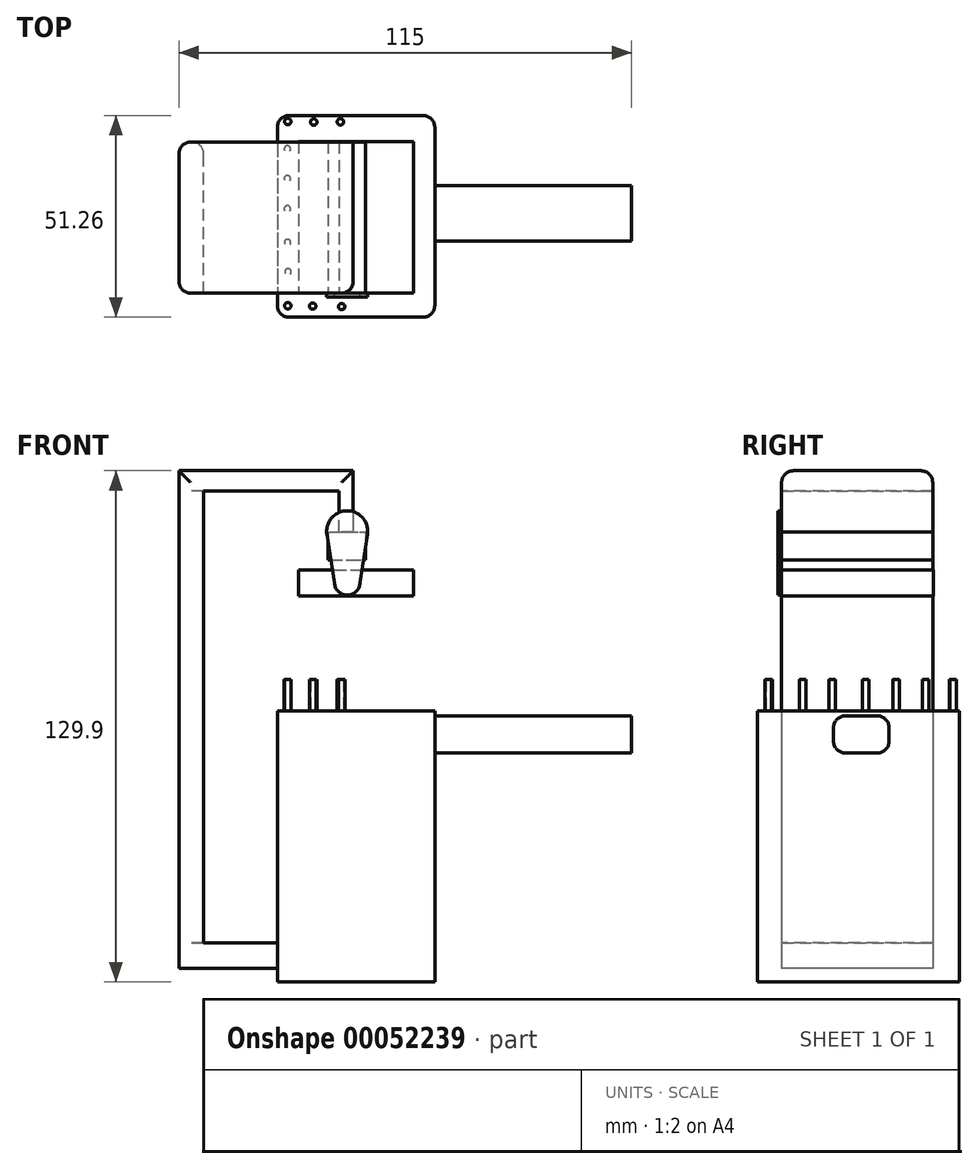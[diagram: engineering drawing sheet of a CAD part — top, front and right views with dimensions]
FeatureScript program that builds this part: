
annotation { "Feature Type Name" : "Feature", "Feature Type Description" : "" }
export const myFeature = defineFeature(function(context is Context, id is Id, definition is map)
    precondition{}
    {
        {
            var Q0;
            Q0=qCreatedBy(makeId("Right.planeOp"),FACE);
            var sketch = newSketch(context, id + "F0", { "sketchPlane" : qUnion([Q0])});
            skLineSegment(sketch, "E0.bottom", {"start": v(7.43, 4.7) * mm, "end": v(-6.69, 4.7) * mm});
            skLineSegment(sketch, "E0.top", {"start": v(7.43, -4.7) * mm, "end": v(-6.69, -4.7) * mm});
            skLineSegment(sketch, "E0.left", {"start": v(7.43, 4.7) * mm, "end": v(7.43, -4.7) * mm});
            skLineSegment(sketch, "E0.right", {"start": v(-6.69, 4.7) * mm, "end": v(-6.69, -4.7) * mm});
            skSolve(sketch);
        }
        {
            var Q0;
            Q0 = qSketchRegion(id + "F0", true);
            extrude(context, id + "F1", {"entities" : qUnion([Q0]), "depth" : 50 * mm});
        }
        {
            var Q0;
            Q0=makeQuery(id+"F1.opExtrude","CAP_FACE",FACE,{"disambiguationData":[OSD([sQuery(id+"F0.wireOp",EDGE,"E0.bottom"),sQuery(id+"F0.wireOp",EDGE,"E0.top"),sQuery(id+"F0.wireOp",EDGE,"E0.left"),sQuery(id+"F0.wireOp",EDGE,"E0.right")])],"isStart":true});
            var sketch = newSketch(context, id + "F2", { "sketchPlane" : qUnion([Q0])});
            skLineSegment(sketch, "E1.bottom", {"start": v(-25.26, 5.94) * mm, "end": v(26, 5.94) * mm});
            skLineSegment(sketch, "E1.top", {"start": v(-25.26, -62.9) * mm, "end": v(26, -62.9) * mm});
            skLineSegment(sketch, "E1.left", {"start": v(-25.26, 5.94) * mm, "end": v(-25.26, -62.9) * mm});
            skLineSegment(sketch, "E1.right", {"start": v(26, 5.94) * mm, "end": v(26, -62.9) * mm});
            skSolve(sketch);
        }
        {
            var Q0;
            Q0 = qSketchRegion(id + "F2", true);
            extrude(context, id + "F3", {"entities" : qUnion([Q0]), "operationType" : NewBodyOperationType.ADD, "depth" : 40 * mm});
        }
        {
            var Q0;
            Q0=makeQuery(id+"F3.opExtrude","CAP_FACE",FACE,{"disambiguationData":[OSD([sQuery(id+"F2.wireOp",EDGE,"E1.bottom"),sQuery(id+"F2.wireOp",EDGE,"E1.top"),sQuery(id+"F2.wireOp",EDGE,"E1.left"),sQuery(id+"F2.wireOp",EDGE,"E1.right")])],"isStart":false});
            var sketch = newSketch(context, id + "F4", { "sketchPlane" : qUnion([Q0])});
            skLineSegment(sketch, "E2.bottom", {"start": v(-18.5, -53) * mm, "end": v(19.88, -53) * mm});
            skLineSegment(sketch, "E2.top", {"start": v(-18.5, -59.44) * mm, "end": v(19.88, -59.44) * mm});
            skLineSegment(sketch, "E2.left", {"start": v(-18.5, -53) * mm, "end": v(-18.5, -59.44) * mm});
            skLineSegment(sketch, "E2.right", {"start": v(19.88, -53) * mm, "end": v(19.88, -59.44) * mm});
            skSolve(sketch);
        }
        {
            var Q0;
            Q0 = qSketchRegion(id + "F4", true);
            extrude(context, id + "F5", {"entities" : qUnion([Q0]), "operationType" : NewBodyOperationType.ADD, "depth" : 25 * mm});
        }
        {
            var Q0;
            Q0=makeQuery(id+"F5.opExtrude","SWEPT_FACE",FACE,{"disambiguationData":[OSD([sQuery(id+"F4.wireOp",EDGE,"E2.bottom")])]});
            var sketch = newSketch(context, id + "F6", { "sketchPlane" : qUnion([Q0])});
            skLineSegment(sketch, "E3.bottom", {"start": v(-58.72, -19.88) * mm, "end": v(-65, -19.88) * mm});
            skLineSegment(sketch, "E3.top", {"start": v(-58.72, 18.5) * mm, "end": v(-65, 18.5) * mm});
            skLineSegment(sketch, "E3.left", {"start": v(-58.72, -19.88) * mm, "end": v(-58.72, 18.5) * mm});
            skLineSegment(sketch, "E3.right", {"start": v(-65, -19.88) * mm, "end": v(-65, 18.5) * mm});
            skSolve(sketch);
        }
        {
            var Q0;
            Q0 = qSketchRegion(id + "F6", true);
            extrude(context, id + "F7", {"entities" : qUnion([Q0]), "operationType" : NewBodyOperationType.ADD, "depth" : 120 * mm});
        }
        {
            var Q0;
            Q0=makeQuery(id+"F7.opExtrude","SWEPT_FACE",FACE,{"disambiguationData":[OSD([sQuery(id+"F6.wireOp",EDGE,"E3.left")])]});
            var sketch = newSketch(context, id + "F8", { "sketchPlane" : qUnion([Q0])});
            skLineSegment(sketch, "E4.bottom", {"start": v(-19.88, 67) * mm, "end": v(18.5, 67) * mm});
            skLineSegment(sketch, "E4.top", {"start": v(-19.88, 61.85) * mm, "end": v(18.5, 61.85) * mm});
            skLineSegment(sketch, "E4.left", {"start": v(-19.88, 67) * mm, "end": v(-19.88, 61.85) * mm});
            skLineSegment(sketch, "E4.right", {"start": v(18.5, 67) * mm, "end": v(18.5, 61.85) * mm});
            skSolve(sketch);
        }
        {
            var Q0;
            Q0 = qSketchRegion(id + "F8", true);
            extrude(context, id + "F9", {"entities" : qUnion([Q0]), "operationType" : NewBodyOperationType.ADD, "depth" : 38 * mm});
        }
        {
            var Q0;
            Q0=makeQuery(id+"F9.opExtrude","SWEPT_FACE",FACE,{"disambiguationData":[OSD([sQuery(id+"F8.wireOp",EDGE,"E4.top")])]});
            var sketch = newSketch(context, id + "F10", { "sketchPlane" : qUnion([Q0])});
            skLineSegment(sketch, "E5.bottom", {"start": v(-20.72, -18.5) * mm, "end": v(-24.3, -18.5) * mm});
            skLineSegment(sketch, "E5.top", {"start": v(-20.72, 19.88) * mm, "end": v(-24.3, 19.88) * mm});
            skLineSegment(sketch, "E5.left", {"start": v(-20.72, -18.5) * mm, "end": v(-20.72, 19.88) * mm});
            skLineSegment(sketch, "E5.right", {"start": v(-24.3, -18.5) * mm, "end": v(-24.3, 19.88) * mm});
            skSolve(sketch);
        }
        {
            var Q0;
            Q0 = qSketchRegion(id + "F10", true);
            extrude(context, id + "F11", {"entities" : qUnion([Q0]), "operationType" : NewBodyOperationType.ADD, "depth" : 15 * mm});
        }
        {
            var Q0;
            Q0=makeQuery(id+"F11.boolean.opBoolean","MERGE",FACE,{"derivedFrom":[makeQuery(id+"F9.boolean.opBoolean","MERGE",FACE,{"derivedFrom":[makeQuery(id+"F7.boolean.opBoolean","MERGE",FACE,{"derivedFrom":[makeQuery(id+"F5.opExtrude","SWEPT_FACE",FACE,{"disambiguationData":[OSD([sQuery(id+"F4.wireOp",EDGE,"E2.right")])]}),makeQuery(id+"F7.opExtrude","SWEPT_FACE",FACE,{"disambiguationData":[OSD([sQuery(id+"F6.wireOp",EDGE,"E3.bottom")])]})]}),makeQuery(id+"F9.opExtrude","SWEPT_FACE",FACE,{"disambiguationData":[OSD([sQuery(id+"F8.wireOp",EDGE,"E4.left")])]})]}),makeQuery(id+"F11.opExtrude","SWEPT_FACE",FACE,{"disambiguationData":[OSD([sQuery(id+"F10.wireOp",EDGE,"E5.top")])]})]});
            var sketch = newSketch(context, id + "F12", { "sketchPlane" : qUnion([Q0])});
            skLineSegment(sketch, "E6.bottom", {"start": v(-27.08, 51.49) * mm, "end": v(-17.55, 51.49) * mm});
            skLineSegment(sketch, "E6.top", {"start": v(-27.08, 44.36) * mm, "end": v(-17.55, 44.36) * mm});
            skLineSegment(sketch, "E6.left", {"start": v(-27.08, 51.49) * mm, "end": v(-27.08, 44.36) * mm});
            skLineSegment(sketch, "E6.right", {"start": v(-17.55, 51.49) * mm, "end": v(-17.55, 44.36) * mm});
            skSolve(sketch);
        }
        {
            var Q0;
            Q0=makeQuery(id+"F12.imprint","IMPRINT",FACE,{"disambiguationData":[TD([[makeQuery(id+"F12.imprint","IMPRINT",EDGE,{"derivedFrom":sQuery(id+"F12.wireOp",EDGE,"E6.top")}),1.0]])]});
            var Q1;
            {var subQ1=sQuery(id+"F10.wireOp",EDGE,"E5.top");var subQ7=makeQuery(id+"F11.opExtrude","CAP_EDGE",EDGE,{"disambiguationData":[OSD([subQ1])],"isStart":false});Q1=makeQuery(id+"F12.imprint","IMPRINT",FACE,{"disambiguationData":[TD([[makeQuery(id+"F12.imprint","IMPRINT",EDGE,{"derivedFrom":subQ7}),-1.0]])]});}
            extrude(context, id + "F13", {"entities" : qUnion([Q0, Q1]), "operationType" : NewBodyOperationType.ADD, "oppositeDirection" : true, "depth" : 38.4 * mm});
        }
        {
            var Q0;
            Q0=makeQuery(id+"F13.boolean.opBoolean","MERGE",FACE,{"derivedFrom":[makeQuery(id+"F11.boolean.opBoolean","MERGE",FACE,{"derivedFrom":[makeQuery(id+"F9.boolean.opBoolean","MERGE",FACE,{"derivedFrom":[makeQuery(id+"F7.boolean.opBoolean","MERGE",FACE,{"derivedFrom":[makeQuery(id+"F5.opExtrude","SWEPT_FACE",FACE,{"disambiguationData":[OSD([sQuery(id+"F4.wireOp",EDGE,"E2.right")])]}),makeQuery(id+"F7.opExtrude","SWEPT_FACE",FACE,{"disambiguationData":[OSD([sQuery(id+"F6.wireOp",EDGE,"E3.bottom")])]})]}),makeQuery(id+"F9.opExtrude","SWEPT_FACE",FACE,{"disambiguationData":[OSD([sQuery(id+"F8.wireOp",EDGE,"E4.left")])]})]}),makeQuery(id+"F11.opExtrude","SWEPT_FACE",FACE,{"disambiguationData":[OSD([sQuery(id+"F10.wireOp",EDGE,"E5.top")])]})]}),makeQuery(id+"F13.opExtrude","CAP_FACE",FACE,{"disambiguationData":[OSD([sQuery(id+"F12.wireOp",EDGE,"E6.bottom"),sQuery(id+"F12.wireOp",EDGE,"E6.top"),sQuery(id+"F12.wireOp",EDGE,"E6.left"),sQuery(id+"F12.wireOp",EDGE,"E6.right")])],"isStart":true})]});
            var sketch = newSketch(context, id + "F14", { "sketchPlane" : qUnion([Q0])});
            skLineSegment(sketch, "E7.bottom", {"start": v(-34.64, 41.85) * mm, "end": v(-5.41, 41.85) * mm});
            skLineSegment(sketch, "E7.top", {"start": v(-34.64, 35.16) * mm, "end": v(-5.41, 35.16) * mm});
            skLineSegment(sketch, "E7.left", {"start": v(-34.64, 41.85) * mm, "end": v(-34.64, 35.16) * mm});
            skLineSegment(sketch, "E7.right", {"start": v(-5.41, 41.85) * mm, "end": v(-5.41, 35.16) * mm});
            skSolve(sketch);
        }
        {
            var Q0;
            Q0 = qSketchRegion(id + "F14", true);
            extrude(context, id + "F15", {"entities" : qUnion([Q0]), "oppositeDirection" : true, "depth" : 38.5 * mm});
        }
        {
            var Q0;
            Q0=makeQuery(id+"F3.opExtrude","SWEPT_FACE",FACE,{"disambiguationData":[OSD([sQuery(id+"F2.wireOp",EDGE,"E1.bottom")])]});
            var sketch = newSketch(context, id + "F16", { "sketchPlane" : qUnion([Q0])});
            skCircle(sketch, "E8", {"center": v(-37.33, 23.74) * mm, "radius": 0.82 * mm});
            skCircle(sketch, "E9", {"center": v(-30.74, 23.6) * mm, "radius": 0.82 * mm});
            skCircle(sketch, "E10", {"center": v(-23.97, 23.65) * mm, "radius": 0.82 * mm});
            skCircle(sketch, "E11", {"center": v(-37.45, 16.76) * mm, "radius": 0.82 * mm});
            skCircle(sketch, "E12", {"center": v(-37.43, 9.2) * mm, "radius": 0.82 * mm});
            skCircle(sketch, "E13", {"center": v(-37.45, 1.53) * mm, "radius": 0.82 * mm});
            skCircle(sketch, "E14", {"center": v(-37.33, -23.08) * mm, "radius": 0.82 * mm});
            skCircle(sketch, "E15", {"center": v(-37.4, -7.02) * mm, "radius": 0.82 * mm});
            skCircle(sketch, "E16", {"center": v(-37.28, -14.5) * mm, "radius": 0.82 * mm});
            skCircle(sketch, "E17", {"center": v(-31.01, -23.17) * mm, "radius": 0.82 * mm});
            skCircle(sketch, "E18", {"center": v(-23.66, -23.3) * mm, "radius": 0.82 * mm});
            skSolve(sketch);
        }
        {
            var Q0;
            Q0 = qSketchRegion(id + "F16", true);
            extrude(context, id + "F17", {"entities" : qUnion([Q0]), "operationType" : NewBodyOperationType.ADD, "depth" : 8 * mm});
        }
        {
            var Q0;
            Q0=makeQuery(id+"F15.opExtrude","CAP_FACE",FACE,{"disambiguationData":[OSD([sQuery(id+"F14.wireOp",EDGE,"E7.bottom"),sQuery(id+"F14.wireOp",EDGE,"E7.top"),sQuery(id+"F14.wireOp",EDGE,"E7.left"),sQuery(id+"F14.wireOp",EDGE,"E7.right")])],"isStart":true});
            var sketch = newSketch(context, id + "F18", { "sketchPlane" : qUnion([Q0])});
            skCircle(sketch, "E19", {"center": v(-22.24, 51.62) * mm, "radius": 5.2 * mm});
            skCircle(sketch, "E20", {"center": v(-22.24, 38.62) * mm, "radius": 3.23 * mm});
            skLineSegment(sketch, "E21", {"start": v(-25.47, 38.5) * mm, "end": v(-27.39, 50.82) * mm});
            skPoint(sketch, "E21.startSnap0", {"position": v(-34.64, 38.5) * mm});
            skLineSegment(sketch, "E22", {"start": v(-19.01, 38.62) * mm, "end": v(-17.1, 50.81) * mm});
            skSolve(sketch);
        }
        {
            var Q0;
            Q0 = qSketchRegion(id + "F18", true);
            extrude(context, id + "F19", {"entities" : qUnion([Q0]), "depth" : 1 * mm});
        }
        {
            var Q0;
            Q0=makeQuery(id+"F7.boolean.opBoolean","MERGE",EDGE,{"derivedFrom":[makeQuery(id+"F5.opExtrude","CAP_EDGE",EDGE,{"disambiguationData":[OSD([sQuery(id+"F4.wireOp",EDGE,"E2.right")])],"isStart":false}),makeQuery(id+"F7.opExtrude","SWEPT_EDGE",EDGE,{"disambiguationData":[OSD([sQuery(id+"F6.wireOp",EDGE,"E3.bottom"),sQuery(id+"F6.wireOp",EDGE,"E3.right")])]})]});
            var Q1;
            Q1=makeQuery(id+"F9.boolean.opBoolean","MERGE",EDGE,{"derivedFrom":[makeQuery(id+"F7.opExtrude","CAP_EDGE",EDGE,{"disambiguationData":[OSD([sQuery(id+"F6.wireOp",EDGE,"E3.bottom")])],"isStart":false}),makeQuery(id+"F9.opExtrude","SWEPT_EDGE",EDGE,{"disambiguationData":[OSD([sQuery(id+"F8.wireOp",EDGE,"E4.bottom"),sQuery(id+"F8.wireOp",EDGE,"E4.left")])]})]});
            var Q2;
            Q2=makeQuery(id+"F11.boolean.opBoolean","MERGE",EDGE,{"derivedFrom":[makeQuery(id+"F9.opExtrude","CAP_EDGE",EDGE,{"disambiguationData":[OSD([sQuery(id+"F8.wireOp",EDGE,"E4.left")])],"isStart":false}),makeQuery(id+"F11.opExtrude","SWEPT_EDGE",EDGE,{"disambiguationData":[OSD([sQuery(id+"F10.wireOp",EDGE,"E5.top"),sQuery(id+"F10.wireOp",EDGE,"E5.left")])]})]});
            var Q3;
            Q3=makeQuery(id+"F3.opExtrude","CAP_EDGE",EDGE,{"disambiguationData":[OSD([sQuery(id+"F2.wireOp",EDGE,"E1.right")])],"isStart":false});
            var Q4;
            Q4=makeQuery(id+"F1.opExtrude","SWEPT_EDGE",EDGE,{"disambiguationData":[OSD([sQuery(id+"F0.wireOp",EDGE,"E0.bottom"),sQuery(id+"F0.wireOp",EDGE,"E0.right")])]});
            var Q5;
            Q5=makeQuery(id+"F1.opExtrude","SWEPT_EDGE",EDGE,{"disambiguationData":[OSD([sQuery(id+"F0.wireOp",EDGE,"E0.top"),sQuery(id+"F0.wireOp",EDGE,"E0.right")])]});
            var Q6;
            Q6=makeQuery(id+"F1.opExtrude","SWEPT_EDGE",EDGE,{"disambiguationData":[OSD([sQuery(id+"F0.wireOp",EDGE,"E0.top"),sQuery(id+"F0.wireOp",EDGE,"E0.left")])]});
            var Q7;
            Q7=makeQuery(id+"F1.opExtrude","SWEPT_EDGE",EDGE,{"disambiguationData":[OSD([sQuery(id+"F0.wireOp",EDGE,"E0.bottom"),sQuery(id+"F0.wireOp",EDGE,"E0.left")])]});
            var Q8;
            Q8=makeQuery(id+"F3.opExtrude","CAP_EDGE",EDGE,{"disambiguationData":[OSD([sQuery(id+"F2.wireOp",EDGE,"E1.left")])],"isStart":false});
            var Q9;
            Q9=makeQuery(id+"F3.opExtrude","CAP_EDGE",EDGE,{"disambiguationData":[OSD([sQuery(id+"F2.wireOp",EDGE,"E1.left")])],"isStart":true});
            var Q10;
            Q10=makeQuery(id+"F3.opExtrude","CAP_EDGE",EDGE,{"disambiguationData":[OSD([sQuery(id+"F2.wireOp",EDGE,"E1.right")])],"isStart":true});
            var Q11;
            Q11=makeQuery(id+"F7.opExtrude","SWEPT_EDGE",EDGE,{"disambiguationData":[OSD([sQuery(id+"F4.wireOp",EDGE,"E2.bottom"),sQuery(id+"F4.wireOp",EDGE,"E2.left"),sQuery(id+"F6.wireOp",EDGE,"E3.top"),sQuery(id+"F6.wireOp",EDGE,"E3.left")])]});
            var Q12;
            Q12=makeQuery(id+"F9.boolean.opBoolean","MERGE",EDGE,{"derivedFrom":[makeQuery(id+"F7.opExtrude","CAP_EDGE",EDGE,{"disambiguationData":[OSD([sQuery(id+"F6.wireOp",EDGE,"E3.top")])],"isStart":false}),makeQuery(id+"F9.opExtrude","SWEPT_EDGE",EDGE,{"disambiguationData":[OSD([sQuery(id+"F8.wireOp",EDGE,"E4.bottom"),sQuery(id+"F8.wireOp",EDGE,"E4.right")])]})]});
            var Q13;
            Q13=makeQuery(id+"F7.boolean.opBoolean","MERGE",EDGE,{"derivedFrom":[makeQuery(id+"F5.opExtrude","CAP_EDGE",EDGE,{"disambiguationData":[OSD([sQuery(id+"F4.wireOp",EDGE,"E2.left")])],"isStart":false}),makeQuery(id+"F7.opExtrude","SWEPT_EDGE",EDGE,{"disambiguationData":[OSD([sQuery(id+"F6.wireOp",EDGE,"E3.top"),sQuery(id+"F6.wireOp",EDGE,"E3.right")])]})]});
            fillet(context, id + "F20", {"entities" : qUnion([Q0, Q1, Q2, Q3, Q4, Q5, Q6, Q7, Q8, Q9, Q10, Q11, Q12, Q13]), "radius" : 3 * mm, "tangentPropagation" : true, "allowEdgeOverflow" : false});
        }
    });
